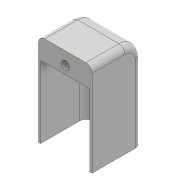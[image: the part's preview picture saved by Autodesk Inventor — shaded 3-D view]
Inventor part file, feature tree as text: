
AUTODESK INVENTOR PART (.ipt)
format: ipt  version: 2017 (Build 210142000, 142)  size: 204,288 bytes
history: native  units: mm
features: sketch x9, extrude x7, fillet x4, projected_geometry x3, hole x1
ambient origin geometry x8: Origin, YZ Plane, XZ Plane, XY Plane, X Axis, Y Axis, Z Axis, Center Point
bodies: Solid1 (feature_tree)
feature tree (24):
  extrude  "Extrusion1"  Depth=10.0mm
  extrude  "Extrusion2"  Depth=9.0mm
  fillet  "Fillet1"  Radius=4.5mm
  hole  "Hole1"  [1 undecoded]
  extrude  "Extrusion3"  Depth=3.0mm
  extrude  "Extrusion4"  Depth=1.0mm
  fillet  "Fillet2"  Radius=1.0mm
  extrude  "Extrusion5"  Depth=35.0mm TaperAngle=0.0deg
  fillet  "Fillet3"  Radius=6.0mm
  fillet  "Fillet4"  Radius=2.0mm
  sketch  "Sketch7"  dims[d26=8.0mm d27=10.0mm d28=0.0mm]
  extrude  "Extrusion6"  Depth=10.0mm TaperAngle=0.0deg
  extrude  "Extrusion7"  Depth=3.0mm
  sketch  "Sketch1"  dims[d0=26.0mm d1=10.0mm]
  sketch  "Sketch2"  dims[d2=14.0mm d3=0.0mm d4=9.0mm d5=4.5mm]
  projected_geometry  "Projected Loop1"
  sketch  "Sketch3"  dims[d6=8.0mm d7=3.0mm d8=0.0mm]
  sketch  "Sketch4"  dims[d9=3.0mm d10=4.1mm]
  projected_geometry  "Projected Loop2"
  sketch  "Sketch5"  dims[d11=4.0mm d12=6.0mm d13=4.0mm d14=2.0mm d15=90.0deg d16=8.0mm d17=20.594885mm d18=1.0mm d19=1.0mm]
  sketch  "Sketch6"  dims[d20=2.0mm d21=35.0mm d22=0.0mm d23=6.0mm d24=2.0mm d25=0.0mm]
  projected_geometry  "Projected Loop3"
  sketch  "Sketch8"  dims[d29=3.0mm d30=3.0mm]
  sketch  "Sketch9"  dims[d31=9.5mm d32=0.0mm d33=20.0mm d34=0.0mm d35=9.5mm d36=0.0mm]
note: 1 required parameter value undecoded (feature->parameter linkage not recoverable at this tier; creation-order binding heuristic only, values carry confidence <= 0.55)
